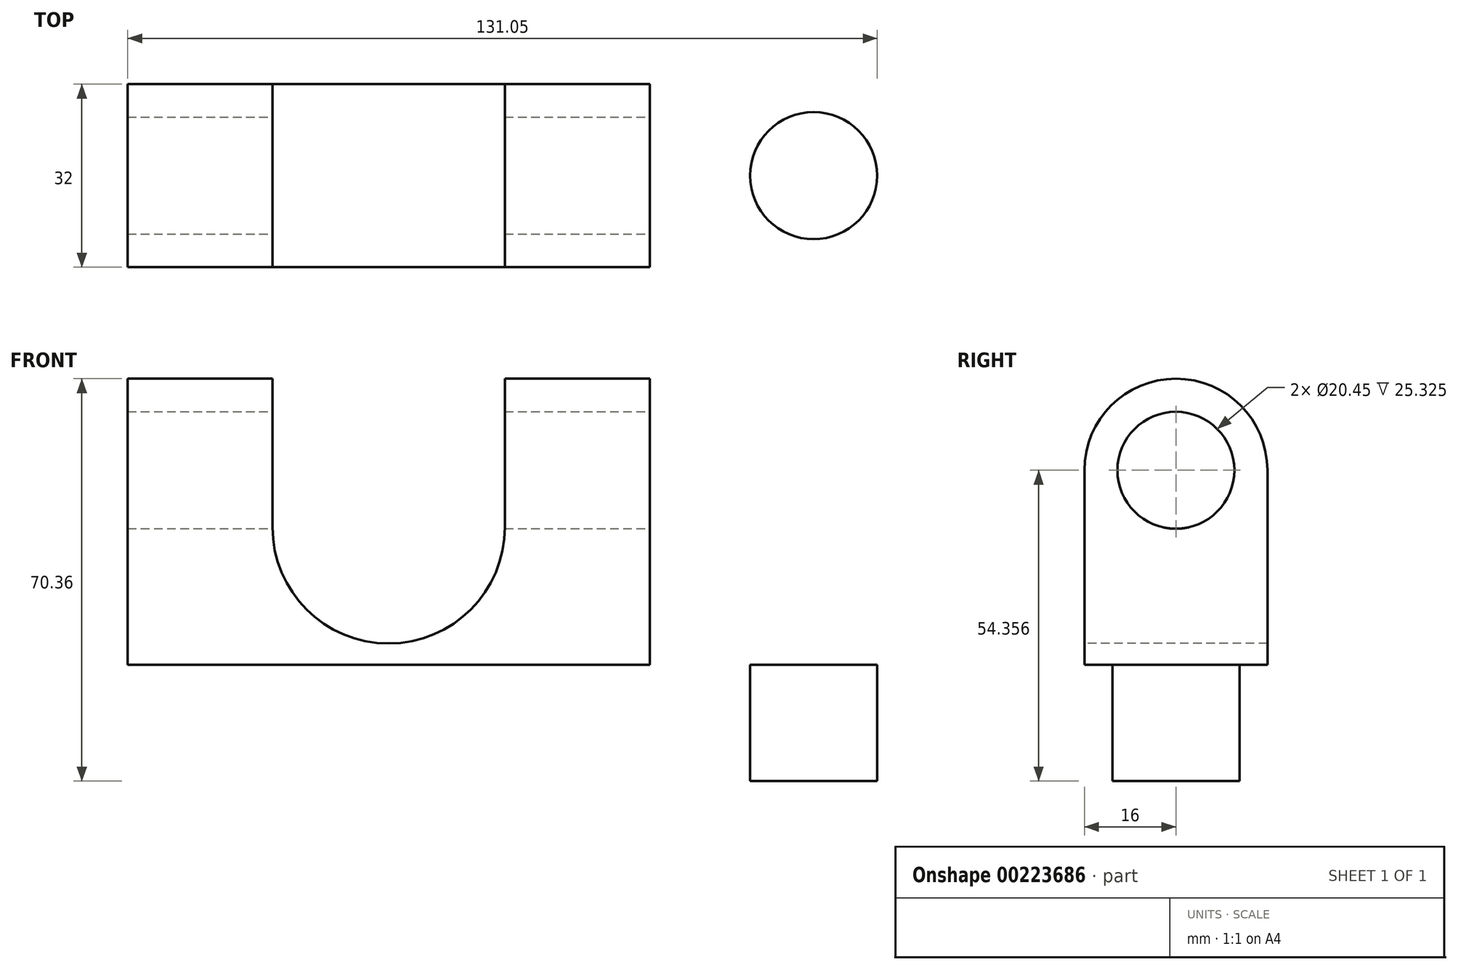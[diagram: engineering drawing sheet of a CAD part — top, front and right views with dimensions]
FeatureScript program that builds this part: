
annotation { "Feature Type Name" : "Feature", "Feature Type Description" : "" }
export const myFeature = defineFeature(function(context is Context, id is Id, definition is map)
    precondition{}
    {
        {
            var Q0;
            Q0=qCreatedBy(makeId("Top.planeOp"),FACE);
            var sketch = newSketch(context, id + "F0", { "sketchPlane" : qUnion([Q0])});
            skLineSegment(sketch, "E0.bottom", {"start": v(70.4, 25.46) * mm, "end": v(-70.4, 25.46) * mm});
            skLineSegment(sketch, "E0.top", {"start": v(70.4, -25.46) * mm, "end": v(-70.4, -25.46) * mm});
            skPoint(sketch, "E0.middle", {"position": v(0, 0) * mm});
            skArc(sketch, "E1", {"start": v(-70.4, 25.46) * mm, "mid": v(-95.87, 0) * mm, "end": v(-70.4, -25.46) * mm});
            skArc(sketch, "E2", {"start": v(70.4, -25.46) * mm, "mid": v(95.87, 0) * mm, "end": v(70.4, 25.46) * mm});
            skSolve(sketch);
        }
        {
            var Q0;
            Q0 = qSketchRegion(id + "F0", true);
            extrude(context, id + "F1", {"entities" : qUnion([Q0]), "depth" : 20.32 * mm});
        }
        {
            var Q0;
            Q0=makeQuery(id+"F1.opExtrude","CAP_FACE",FACE,{"disambiguationData":[OSD([sQuery(id+"F0.wireOp",EDGE,"E0.bottom"),sQuery(id+"F0.wireOp",EDGE,"E0.top"),sQuery(id+"F0.wireOp",EDGE,"E1"),sQuery(id+"F0.wireOp",EDGE,"E2")])],"isStart":false});
            var sketch = newSketch(context, id + "F2", { "sketchPlane" : qUnion([Q0])});
            skCircle(sketch, "E3", {"center": v(-74.3, 0) * mm, "radius": 11.1 * mm});
            skCircle(sketch, "E4.MirrorC", {"center": v(74.3, 0) * mm, "radius": 11.1 * mm});
            skSolve(sketch);
        }
        {
            var Q0;
            Q0=makeQuery(id+"F2.imprint","IMPRINT",FACE,{"disambiguationData":[TD([[makeQuery(id+"F2.imprint","IMPRINT",EDGE,{"derivedFrom":sQuery(id+"F2.wireOp",EDGE,"E4.MirrorC")}),-1.0]])]});
            var Q1;
            Q1=makeQuery(id+"F2.imprint","IMPRINT",FACE,{"disambiguationData":[TD([[makeQuery(id+"F2.imprint","IMPRINT",EDGE,{"derivedFrom":sQuery(id+"F2.wireOp",EDGE,"E3")}),1.0]])]});
            extrude(context, id + "F3", {"entities" : qUnion([Q0, Q1]), "operationType" : NewBodyOperationType.REMOVE, "oppositeDirection" : true, "depth" : 25.4 * mm});
        }
        {
            var Q0;
            Q0=makeQuery(id+"F1.opExtrude","CAP_FACE",FACE,{"disambiguationData":[OSD([sQuery(id+"F0.wireOp",EDGE,"E0.bottom"),sQuery(id+"F0.wireOp",EDGE,"E0.top"),sQuery(id+"F0.wireOp",EDGE,"E1"),sQuery(id+"F0.wireOp",EDGE,"E2")])],"isStart":false});
            var sketch = newSketch(context, id + "F4", { "sketchPlane" : qUnion([Q0])});
            skLineSegment(sketch, "E5.bottom", {"start": v(45.64, 16) * mm, "end": v(-45.64, 16) * mm});
            skLineSegment(sketch, "E5.top", {"start": v(45.64, -16) * mm, "end": v(-45.64, -16) * mm});
            skLineSegment(sketch, "E5.left", {"start": v(45.64, 16) * mm, "end": v(45.64, -16) * mm});
            skLineSegment(sketch, "E5.right", {"start": v(-45.64, 16) * mm, "end": v(-45.64, -16) * mm});
            skPoint(sketch, "E5.middle", {"position": v(0, 0) * mm});
            skSolve(sketch);
        }
        {
            var Q0;
            Q0 = qSketchRegion(id + "F4", true);
            extrude(context, id + "F5", {"entities" : qUnion([Q0]), "operationType" : NewBodyOperationType.ADD, "depth" : 34.04 * mm});
        }
        {
            var Q0;
            Q0=makeQuery(id+"F5.opExtrude","SWEPT_FACE",FACE,{"disambiguationData":[OSD([sQuery(id+"F4.wireOp",EDGE,"E5.left")])]});
            var sketch = newSketch(context, id + "F6", { "sketchPlane" : qUnion([Q0])});
            skCircle(sketch, "E6", {"center": v(0, 54.36) * mm, "radius": 16 * mm});
            skSolve(sketch);
        }
        {
            var Q0;
            Q0 = qSketchRegion(id + "F6", true);
            var Q1;
            Q1=makeQuery(id+"F5.opExtrude","CAP_VERTEX",VERTEX,{"disambiguationData":[OSD([sQuery(id+"F4.wireOp",EDGE,"E5.top"),sQuery(id+"F4.wireOp",EDGE,"E5.right")])],"isStart":false});
            extrude(context, id + "F7", {"entities" : qUnion([Q0]), "operationType" : NewBodyOperationType.ADD, "endBound" : BoundingType.UP_TO_VERTEX, "oppositeDirection" : true, "endBoundEntityVertex" : qUnion([Q1]), "depth" : 92.2 * mm});
        }
        {
            var Q0;
            Q0=qCreatedBy(makeId("Front.planeOp"),FACE);
            var sketch = newSketch(context, id + "F8", { "sketchPlane" : qUnion([Q0])});
            skLineSegment(sketch, "E7.top", {"start": v(20.32, 96.7) * mm, "end": v(-20.32, 96.7) * mm});
            skLineSegment(sketch, "E7.left", {"start": v(20.32, 44.39) * mm, "end": v(20.32, 96.7) * mm});
            skLineSegment(sketch, "E7.right", {"start": v(-20.32, 44.39) * mm, "end": v(-20.32, 96.7) * mm});
            skPoint(sketch, "E7.middle", {"position": v(0, 70.55) * mm});
            skArc(sketch, "E8", {"start": v(-20.32, 44.39) * mm, "mid": v(0, 24.07) * mm, "end": v(20.32, 44.39) * mm});
            skSolve(sketch);
        }
        {
            var Q0;
            Q0 = qSketchRegion(id + "F8", true);
            extrude(context, id + "F9", {"entities" : qUnion([Q0]), "operationType" : NewBodyOperationType.REMOVE, "endBound" : BoundingType.SYMMETRIC, "oppositeDirection" : true, "depth" : 67.06 * mm});
        }
        {
            var Q0;
            Q0=makeQuery(id+"F7.boolean.opBoolean","MERGE",FACE,{"derivedFrom":[makeQuery(id+"F5.opExtrude","SWEPT_FACE",FACE,{"disambiguationData":[OSD([sQuery(id+"F4.wireOp",EDGE,"E5.left")])]}),makeQuery(id+"F7.opExtrude","CAP_FACE",FACE,{"disambiguationData":[OSD([sQuery(id+"F6.wireOp",EDGE,"E6")])],"isStart":true})]});
            var sketch = newSketch(context, id + "F10", { "sketchPlane" : qUnion([Q0])});
            skCircle(sketch, "E9", {"center": v(0, 54.36) * mm, "radius": 10.23 * mm});
            skSolve(sketch);
        }
        {
            var Q0;
            Q0 = qSketchRegion(id + "F10", true);
            extrude(context, id + "F11", {"entities" : qUnion([Q0]), "operationType" : NewBodyOperationType.REMOVE, "oppositeDirection" : true, "depth" : 105.4 * mm});
        }
    });
